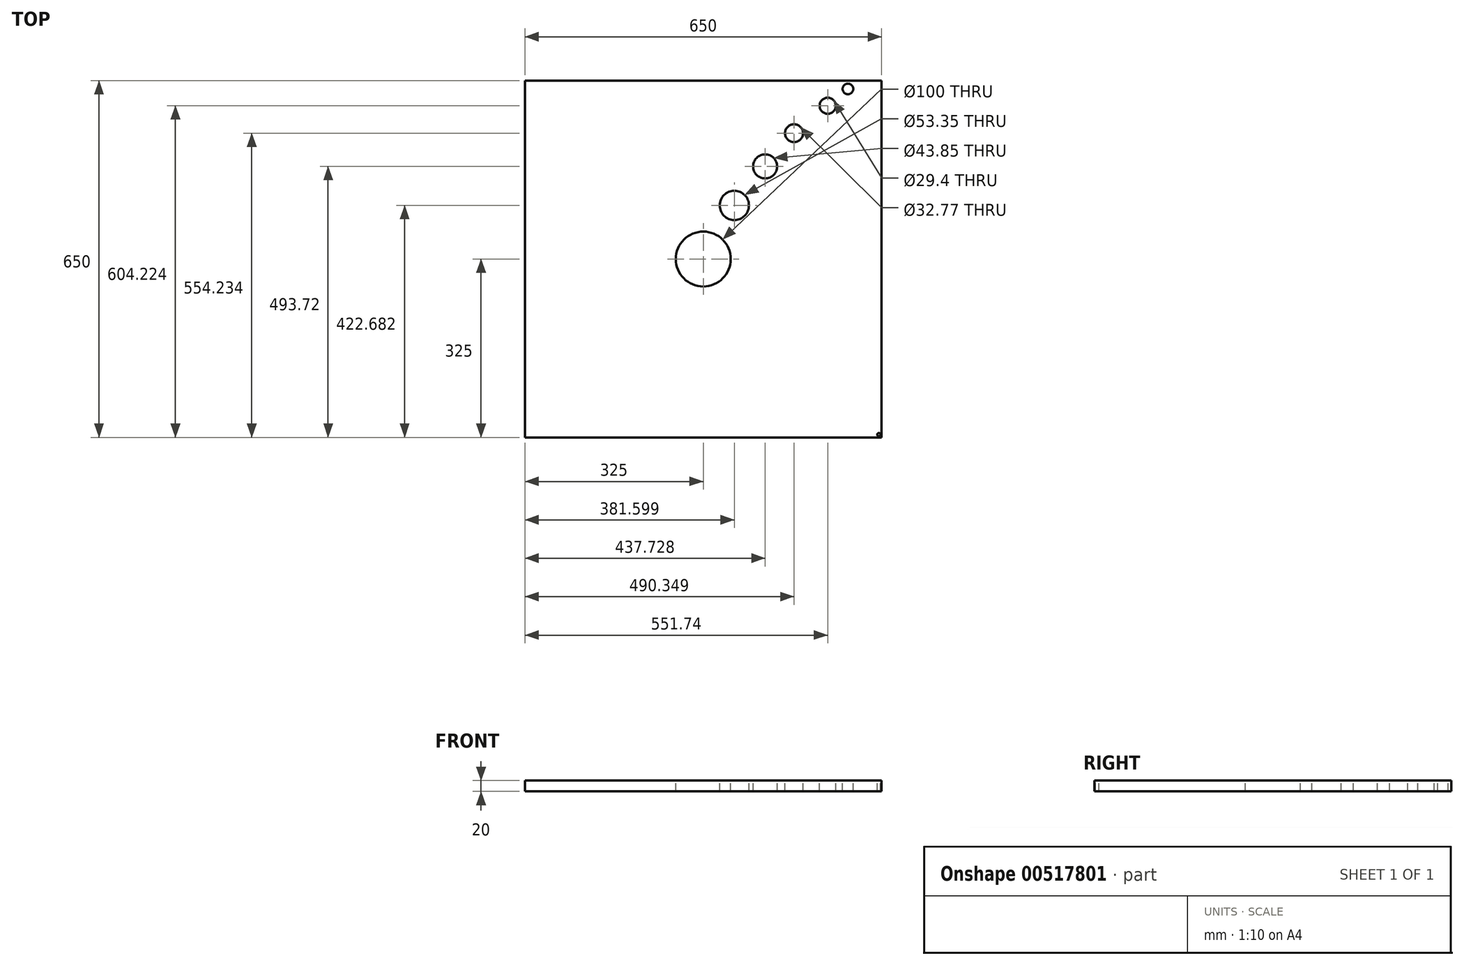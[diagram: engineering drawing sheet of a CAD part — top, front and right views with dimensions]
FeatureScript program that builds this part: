
annotation { "Feature Type Name" : "Feature", "Feature Type Description" : "" }
export const myFeature = defineFeature(function(context is Context, id is Id, definition is map)
    precondition{}
    {
        {
            var Q0;
            Q0=qCreatedBy(makeId("Top.planeOp"),FACE);
            var sketch = newSketch(context, id + "F0", { "sketchPlane" : qUnion([Q0])});
            skLineSegment(sketch, "E0.bottom", {"start": v(0, 0) * mm, "end": v(650, 0) * mm});
            skLineSegment(sketch, "E0.top", {"start": v(0, -650) * mm, "end": v(650, -650) * mm});
            skLineSegment(sketch, "E0.left", {"start": v(0, 0) * mm, "end": v(0, -650) * mm});
            skLineSegment(sketch, "E0.right", {"start": v(650, 0) * mm, "end": v(650, -650) * mm});
            skSolve(sketch);
        }
        {
            var Q0;
            Q0=makeQuery(id+"F0.imprint","IMPRINT",FACE,{"disambiguationData":[TD([[makeQuery(id+"F0.imprint","IMPRINT",EDGE,{"derivedFrom":sQuery(id+"F0.wireOp",EDGE,"E0.bottom")}),-1.0]])]});
            extrude(context, id + "F1", {"entities" : qUnion([Q0]), "depth" : 20 * mm, "offsetDistance" : 25 * mm});
        }
        {
            var Q0;
            Q0=makeQuery(id+"F1.opExtrude","CAP_FACE",FACE,{"disambiguationData":[OSD([sQuery(id+"F0.wireOp",EDGE,"E0.bottom"),sQuery(id+"F0.wireOp",EDGE,"E0.top"),sQuery(id+"F0.wireOp",EDGE,"E0.left"),sQuery(id+"F0.wireOp",EDGE,"E0.right")])],"isStart":false});
            var sketch = newSketch(context, id + "F2", { "sketchPlane" : qUnion([Q0])});
            skCircle(sketch, "E1", {"center": v(325, -325) * mm, "radius": 50 * mm});
            skSolve(sketch);
        }
        {
            var Q0;
            Q0=makeQuery(id+"F2.imprint","IMPRINT",FACE,{"disambiguationData":[TD([[makeQuery(id+"F2.imprint","IMPRINT",EDGE,{"derivedFrom":sQuery(id+"F2.wireOp",EDGE,"E1")}),1.0]])]});
            extrude(context, id + "F3", {"entities" : qUnion([Q0]), "operationType" : NewBodyOperationType.REMOVE, "oppositeDirection" : true, "depth" : 25 * mm, "offsetDistance" : 25 * mm});
        }
        {
            var Q0;
            Q0=makeQuery(id+"F1.opExtrude","CAP_FACE",FACE,{"disambiguationData":[OSD([sQuery(id+"F0.wireOp",EDGE,"E0.bottom"),sQuery(id+"F0.wireOp",EDGE,"E0.top"),sQuery(id+"F0.wireOp",EDGE,"E0.left"),sQuery(id+"F0.wireOp",EDGE,"E0.right")])],"isStart":false});
            var sketch = newSketch(context, id + "F4", { "sketchPlane" : qUnion([Q0])});
            skCircle(sketch, "E2", {"center": v(381.6, -227.32) * mm, "radius": 26.67 * mm});
            skSolve(sketch);
        }
        {
            var Q0;
            Q0=makeQuery(id+"F4.imprint","IMPRINT",FACE,{"disambiguationData":[TD([[makeQuery(id+"F4.imprint","IMPRINT",EDGE,{"derivedFrom":sQuery(id+"F4.wireOp",EDGE,"E2")}),-1.0]])]});
            var sketch = newSketch(context, id + "F5", { "sketchPlane" : qUnion([Q0])});
            skCircle(sketch, "E3", {"center": v(437.73, -156.28) * mm, "radius": 21.93 * mm});
            skSolve(sketch);
        }
        {
            var Q0;
            Q0=makeQuery(id+"F4.imprint","IMPRINT",FACE,{"disambiguationData":[TD([[makeQuery(id+"F4.imprint","IMPRINT",EDGE,{"derivedFrom":sQuery(id+"F4.wireOp",EDGE,"E2")}),-1.0]])]});
            var sketch = newSketch(context, id + "F6", { "sketchPlane" : qUnion([Q0])});
            skCircle(sketch, "E4", {"center": v(490.35, -95.77) * mm, "radius": 16.38 * mm});
            skSolve(sketch);
        }
        {
            var Q0;
            Q0=makeQuery(id+"F4.imprint","IMPRINT",FACE,{"disambiguationData":[TD([[makeQuery(id+"F4.imprint","IMPRINT",EDGE,{"derivedFrom":sQuery(id+"F4.wireOp",EDGE,"E2")}),-1.0]])]});
            var sketch = newSketch(context, id + "F7", { "sketchPlane" : qUnion([Q0])});
            skCircle(sketch, "E5", {"center": v(551.74, -45.78) * mm, "radius": 14.7 * mm});
            skSolve(sketch);
        }
        {
            var Q0;
            Q0=makeQuery(id+"F4.imprint","IMPRINT",FACE,{"disambiguationData":[TD([[makeQuery(id+"F4.imprint","IMPRINT",EDGE,{"derivedFrom":sQuery(id+"F4.wireOp",EDGE,"E2")}),-1.0]])]});
            var sketch = newSketch(context, id + "F8", { "sketchPlane" : qUnion([Q0])});
            skCircle(sketch, "E6", {"center": v(588.57, -15.08) * mm, "radius": 9.69 * mm});
            skSolve(sketch);
        }
        {
            var Q0;
            Q0=makeQuery(id+"F4.imprint","IMPRINT",FACE,{"disambiguationData":[TD([[makeQuery(id+"F4.imprint","IMPRINT",EDGE,{"derivedFrom":sQuery(id+"F4.wireOp",EDGE,"E2")}),1.0]])]});
            extrude(context, id + "F9", {"entities" : qUnion([Q0]), "operationType" : NewBodyOperationType.REMOVE, "oppositeDirection" : true, "depth" : 25 * mm, "offsetDistance" : 25 * mm});
        }
        {
            var Q0;
            Q0=makeQuery(id+"F5.imprint","IMPRINT",FACE,{"disambiguationData":[TD([[makeQuery(id+"F5.imprint","IMPRINT",EDGE,{"derivedFrom":sQuery(id+"F5.wireOp",EDGE,"E3")}),1.0]])]});
            extrude(context, id + "F10", {"entities" : qUnion([Q0]), "operationType" : NewBodyOperationType.REMOVE, "oppositeDirection" : true, "depth" : 25 * mm, "offsetDistance" : 25 * mm});
        }
        {
            var Q0;
            Q0=makeQuery(id+"F6.imprint","IMPRINT",FACE,{"disambiguationData":[TD([[makeQuery(id+"F6.imprint","IMPRINT",EDGE,{"derivedFrom":sQuery(id+"F6.wireOp",EDGE,"E4")}),1.0]])]});
            extrude(context, id + "F11", {"entities" : qUnion([Q0]), "operationType" : NewBodyOperationType.ADD, "depth" : 25 * mm, "offsetDistance" : 25 * mm});
        }
        {
            var Q0;
            Q0=makeQuery(id+"F7.imprint","IMPRINT",FACE,{"disambiguationData":[TD([[makeQuery(id+"F7.imprint","IMPRINT",EDGE,{"derivedFrom":sQuery(id+"F7.wireOp",EDGE,"E5")}),1.0]])]});
            extrude(context, id + "F12", {"entities" : qUnion([Q0]), "operationType" : NewBodyOperationType.REMOVE, "oppositeDirection" : true, "depth" : 25 * mm, "offsetDistance" : 25 * mm});
        }
        {
            var Q0;
            Q0=makeQuery(id+"F8.imprint","IMPRINT",FACE,{"disambiguationData":[TD([[makeQuery(id+"F8.imprint","IMPRINT",EDGE,{"derivedFrom":sQuery(id+"F8.wireOp",EDGE,"E6")}),1.0]])]});
            extrude(context, id + "F13", {"entities" : qUnion([Q0]), "operationType" : NewBodyOperationType.REMOVE, "oppositeDirection" : true, "depth" : 25 * mm, "offsetDistance" : 25 * mm});
        }
        {
            var Q0;
            Q0=makeQuery(id+"F11.opExtrude","CAP_FACE",FACE,{"disambiguationData":[OSD([sQuery(id+"F6.wireOp",EDGE,"E4")])],"isStart":false});
            extrude(context, id + "F14", {"entities" : qUnion([Q0]), "operationType" : NewBodyOperationType.REMOVE, "oppositeDirection" : true, "depth" : 50 * mm, "offsetDistance" : 25 * mm});
        }
        {
            var Q0;
            Q0=makeQuery(id+"F1.opExtrude","CAP_FACE",FACE,{"disambiguationData":[OSD([sQuery(id+"F0.wireOp",EDGE,"E0.bottom"),sQuery(id+"F0.wireOp",EDGE,"E0.top"),sQuery(id+"F0.wireOp",EDGE,"E0.left"),sQuery(id+"F0.wireOp",EDGE,"E0.right")])],"isStart":false});
            var sketch = newSketch(context, id + "F15", { "sketchPlane" : qUnion([Q0])});
            skCircle(sketch, "E7", {"center": v(645, -645) * mm, "radius": 3 * mm});
            skSolve(sketch);
        }
        {
            var Q0;
            Q0=makeQuery(id+"F15.imprint","IMPRINT",FACE,{"disambiguationData":[TD([[makeQuery(id+"F15.imprint","IMPRINT",EDGE,{"derivedFrom":sQuery(id+"F15.wireOp",EDGE,"E7")}),1.0]])]});
            extrude(context, id + "F16", {"entities" : qUnion([Q0]), "operationType" : NewBodyOperationType.REMOVE, "oppositeDirection" : true, "depth" : 25 * mm, "offsetDistance" : 25 * mm});
        }
    });
